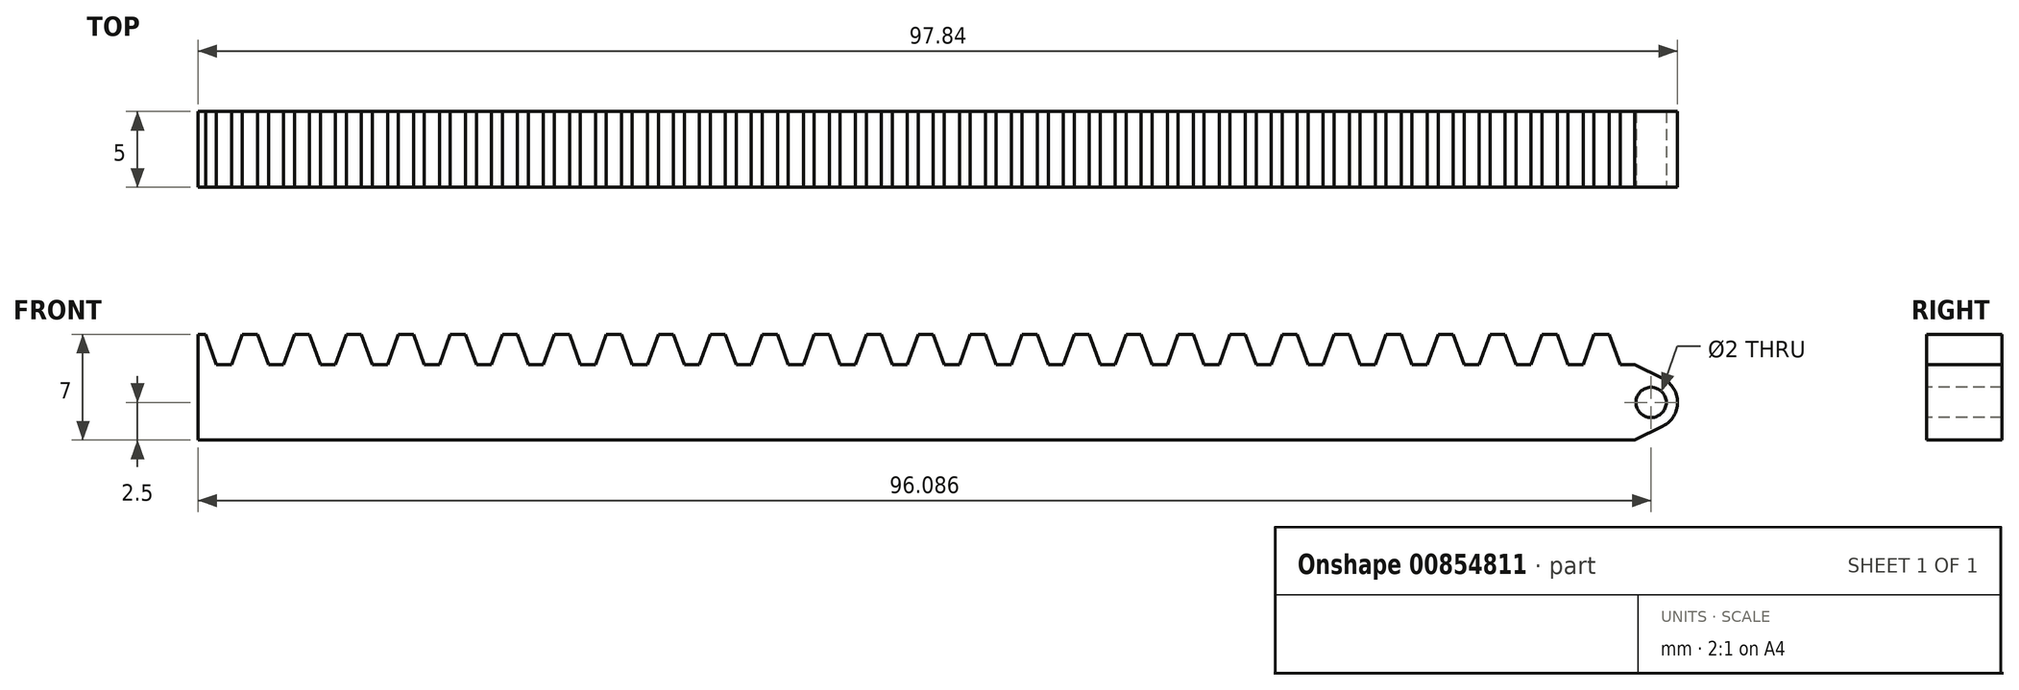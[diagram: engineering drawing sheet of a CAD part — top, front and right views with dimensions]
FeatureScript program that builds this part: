
annotation { "Feature Type Name" : "Feature", "Feature Type Description" : "" }
export const myFeature = defineFeature(function(context is Context, id is Id, definition is map)
    precondition{}
    {
        {
            var Q0;
            Q0=qCreatedBy(makeId("Front.planeOp"),FACE);
            var sketch = newSketch(context, id + "F0", { "sketchPlane" : qUnion([Q0])});
            skLineSegment(sketch, "E0", {"start": v(-54.36, 0) * mm, "end": v(55.64, 0) * mm});
            skLineSegment(sketch, "E1", {"start": v(-54.36, 0) * mm, "end": v(-54.36, 2) * mm});
            skLineSegment(sketch, "E2", {"start": v(-50.92, 4.03) * mm, "end": v(-50.92, 2) * mm, "construction": true});
            skLineSegment(sketch, "E3.MirrorCS", {"start": v(-47.49, 2) * mm, "end": v(-50.92, 2) * mm, "construction": true});
            skLineSegment(sketch, "E4", {"start": v(-54.36, 2) * mm, "end": v(-54.36, 3.15) * mm, "construction": true});
            skLineSegment(sketch, "E5", {"start": v(-54.36, 2) * mm, "end": v(-53.86, 2) * mm});
            skLineSegment(sketch, "E6", {"start": v(-52.64, 0) * mm, "end": v(-52.14, 0) * mm});
            skLineSegment(sketch, "E7", {"start": v(-52.64, 0) * mm, "end": v(-53.14, 0) * mm});
            skLineSegment(sketch, "E8", {"start": v(-50.92, 2) * mm, "end": v(-51.42, 2) * mm});
            skLineSegment(sketch, "E9", {"start": v(-54.36, 3.15) * mm, "end": v(-50.92, 3.15) * mm, "construction": true});
            skLineSegment(sketch, "E10", {"start": v(-52.64, 3.15) * mm, "end": v(-52.64, -0.78) * mm, "construction": true});
            skLineSegment(sketch, "E11", {"start": v(-53.86, 2) * mm, "end": v(-53.14, 0) * mm});
            skLineSegment(sketch, "E12", {"start": v(-52.14, 0) * mm, "end": v(-51.42, 2) * mm});
            skLineSegment(sketch, "E13.1.0.0", {"start": v(-48.7, 0) * mm, "end": v(-47.99, 2) * mm});
            skLineSegment(sketch, "E13.1.0.1", {"start": v(-50.92, 2) * mm, "end": v(-50.42, 2) * mm});
            skLineSegment(sketch, "E13.1.0.2", {"start": v(-50.42, 2) * mm, "end": v(-49.7, 0) * mm});
            skLineSegment(sketch, "E13.1.0.3", {"start": v(-49.2, 0) * mm, "end": v(-49.7, 0) * mm});
            skLineSegment(sketch, "E13.1.0.4", {"start": v(-49.2, 0) * mm, "end": v(-48.7, 0) * mm});
            skLineSegment(sketch, "E13.1.0.5", {"start": v(-47.49, 2) * mm, "end": v(-47.99, 2) * mm});
            skLineSegment(sketch, "E13.2.0.0", {"start": v(-45.27, 0) * mm, "end": v(-44.55, 2) * mm});
            skLineSegment(sketch, "E13.2.0.1", {"start": v(-47.49, 2) * mm, "end": v(-46.99, 2) * mm});
            skLineSegment(sketch, "E13.2.0.2", {"start": v(-46.99, 2) * mm, "end": v(-46.27, 0) * mm});
            skLineSegment(sketch, "E13.2.0.3", {"start": v(-45.77, 0) * mm, "end": v(-46.27, 0) * mm});
            skLineSegment(sketch, "E13.2.0.4", {"start": v(-45.77, 0) * mm, "end": v(-45.27, 0) * mm});
            skLineSegment(sketch, "E13.2.0.5", {"start": v(-44.05, 2) * mm, "end": v(-44.55, 2) * mm});
            skLineSegment(sketch, "E13.3.0.0", {"start": v(-41.83, 0) * mm, "end": v(-41.11, 2) * mm});
            skLineSegment(sketch, "E13.3.0.1", {"start": v(-44.05, 2) * mm, "end": v(-43.55, 2) * mm});
            skLineSegment(sketch, "E13.3.0.2", {"start": v(-43.55, 2) * mm, "end": v(-42.83, 0) * mm});
            skLineSegment(sketch, "E13.3.0.3", {"start": v(-42.33, 0) * mm, "end": v(-42.83, 0) * mm});
            skLineSegment(sketch, "E13.3.0.4", {"start": v(-42.33, 0) * mm, "end": v(-41.83, 0) * mm});
            skLineSegment(sketch, "E13.3.0.5", {"start": v(-40.61, 2) * mm, "end": v(-41.11, 2) * mm});
            skLineSegment(sketch, "E13.4.0.0", {"start": v(-38.4, 0) * mm, "end": v(-37.67, 2) * mm});
            skLineSegment(sketch, "E13.4.0.1", {"start": v(-40.61, 2) * mm, "end": v(-40.11, 2) * mm});
            skLineSegment(sketch, "E13.4.0.2", {"start": v(-40.11, 2) * mm, "end": v(-39.4, 0) * mm});
            skLineSegment(sketch, "E13.4.0.3", {"start": v(-38.9, 0) * mm, "end": v(-39.4, 0) * mm});
            skLineSegment(sketch, "E13.4.0.4", {"start": v(-38.9, 0) * mm, "end": v(-38.4, 0) * mm});
            skLineSegment(sketch, "E13.4.0.5", {"start": v(-37.17, 2) * mm, "end": v(-37.67, 2) * mm});
            skLineSegment(sketch, "E13.5.0.0", {"start": v(-34.95, 0) * mm, "end": v(-34.24, 2) * mm});
            skLineSegment(sketch, "E13.5.0.1", {"start": v(-37.17, 2) * mm, "end": v(-36.67, 2) * mm});
            skLineSegment(sketch, "E13.5.0.2", {"start": v(-36.67, 2) * mm, "end": v(-35.95, 0) * mm});
            skLineSegment(sketch, "E13.5.0.3", {"start": v(-35.45, 0) * mm, "end": v(-35.95, 0) * mm});
            skLineSegment(sketch, "E13.5.0.4", {"start": v(-35.45, 0) * mm, "end": v(-34.95, 0) * mm});
            skLineSegment(sketch, "E13.5.0.5", {"start": v(-33.74, 2) * mm, "end": v(-34.24, 2) * mm});
            skLineSegment(sketch, "E13.6.0.0", {"start": v(-31.52, 0) * mm, "end": v(-30.8, 2) * mm});
            skLineSegment(sketch, "E13.6.0.1", {"start": v(-33.74, 2) * mm, "end": v(-33.24, 2) * mm});
            skLineSegment(sketch, "E13.6.0.2", {"start": v(-33.24, 2) * mm, "end": v(-32.52, 0) * mm});
            skLineSegment(sketch, "E13.6.0.3", {"start": v(-32.02, 0) * mm, "end": v(-32.52, 0) * mm});
            skLineSegment(sketch, "E13.6.0.4", {"start": v(-32.02, 0) * mm, "end": v(-31.52, 0) * mm});
            skLineSegment(sketch, "E13.6.0.5", {"start": v(-30.3, 2) * mm, "end": v(-30.8, 2) * mm});
            skLineSegment(sketch, "E13.7.0.0", {"start": v(-28.08, 0) * mm, "end": v(-27.36, 2) * mm});
            skLineSegment(sketch, "E13.7.0.1", {"start": v(-30.3, 2) * mm, "end": v(-29.8, 2) * mm});
            skLineSegment(sketch, "E13.7.0.2", {"start": v(-29.8, 2) * mm, "end": v(-29.08, 0) * mm});
            skLineSegment(sketch, "E13.7.0.3", {"start": v(-28.58, 0) * mm, "end": v(-29.08, 0) * mm});
            skLineSegment(sketch, "E13.7.0.4", {"start": v(-28.58, 0) * mm, "end": v(-28.08, 0) * mm});
            skLineSegment(sketch, "E13.7.0.5", {"start": v(-26.86, 2) * mm, "end": v(-27.36, 2) * mm});
            skLineSegment(sketch, "E13.8.0.0", {"start": v(-24.64, 0) * mm, "end": v(-23.92, 2) * mm});
            skLineSegment(sketch, "E13.8.0.1", {"start": v(-26.86, 2) * mm, "end": v(-26.36, 2) * mm});
            skLineSegment(sketch, "E13.8.0.2", {"start": v(-26.36, 2) * mm, "end": v(-25.64, 0) * mm});
            skLineSegment(sketch, "E13.8.0.3", {"start": v(-25.14, 0) * mm, "end": v(-25.64, 0) * mm});
            skLineSegment(sketch, "E13.8.0.4", {"start": v(-25.14, 0) * mm, "end": v(-24.64, 0) * mm});
            skLineSegment(sketch, "E13.8.0.5", {"start": v(-23.42, 2) * mm, "end": v(-23.92, 2) * mm});
            skLineSegment(sketch, "E13.9.0.0", {"start": v(-21.2, 0) * mm, "end": v(-20.49, 2) * mm});
            skLineSegment(sketch, "E13.9.0.1", {"start": v(-23.42, 2) * mm, "end": v(-22.92, 2) * mm});
            skLineSegment(sketch, "E13.9.0.2", {"start": v(-22.92, 2) * mm, "end": v(-22.2, 0) * mm});
            skLineSegment(sketch, "E13.9.0.3", {"start": v(-21.7, 0) * mm, "end": v(-22.2, 0) * mm});
            skLineSegment(sketch, "E13.9.0.4", {"start": v(-21.7, 0) * mm, "end": v(-21.2, 0) * mm});
            skLineSegment(sketch, "E13.9.0.5", {"start": v(-19.99, 2) * mm, "end": v(-20.49, 2) * mm});
            skLineSegment(sketch, "E13.10.0.0", {"start": v(-17.77, 0) * mm, "end": v(-17.05, 2) * mm});
            skLineSegment(sketch, "E13.10.0.1", {"start": v(-19.99, 2) * mm, "end": v(-19.49, 2) * mm});
            skLineSegment(sketch, "E13.10.0.2", {"start": v(-19.49, 2) * mm, "end": v(-18.77, 0) * mm});
            skLineSegment(sketch, "E13.10.0.3", {"start": v(-18.27, 0) * mm, "end": v(-18.77, 0) * mm});
            skLineSegment(sketch, "E13.10.0.4", {"start": v(-18.27, 0) * mm, "end": v(-17.77, 0) * mm});
            skLineSegment(sketch, "E13.10.0.5", {"start": v(-16.55, 2) * mm, "end": v(-17.05, 2) * mm});
            skLineSegment(sketch, "E13.11.0.0", {"start": v(-14.33, 0) * mm, "end": v(-13.61, 2) * mm});
            skLineSegment(sketch, "E13.11.0.1", {"start": v(-16.55, 2) * mm, "end": v(-16.05, 2) * mm});
            skLineSegment(sketch, "E13.11.0.2", {"start": v(-16.05, 2) * mm, "end": v(-15.33, 0) * mm});
            skLineSegment(sketch, "E13.11.0.3", {"start": v(-14.83, 0) * mm, "end": v(-15.33, 0) * mm});
            skLineSegment(sketch, "E13.11.0.4", {"start": v(-14.83, 0) * mm, "end": v(-14.33, 0) * mm});
            skLineSegment(sketch, "E13.11.0.5", {"start": v(-13.11, 2) * mm, "end": v(-13.61, 2) * mm});
            skLineSegment(sketch, "E13.12.0.0", {"start": v(-10.9, 0) * mm, "end": v(-10.17, 2) * mm});
            skLineSegment(sketch, "E13.12.0.1", {"start": v(-13.11, 2) * mm, "end": v(-12.61, 2) * mm});
            skLineSegment(sketch, "E13.12.0.2", {"start": v(-12.61, 2) * mm, "end": v(-11.9, 0) * mm});
            skLineSegment(sketch, "E13.12.0.3", {"start": v(-11.4, 0) * mm, "end": v(-11.9, 0) * mm});
            skLineSegment(sketch, "E13.12.0.4", {"start": v(-11.4, 0) * mm, "end": v(-10.9, 0) * mm});
            skLineSegment(sketch, "E13.12.0.5", {"start": v(-9.67, 2) * mm, "end": v(-10.17, 2) * mm});
            skLineSegment(sketch, "E13.13.0.0", {"start": v(-7.45, 0) * mm, "end": v(-6.74, 2) * mm});
            skLineSegment(sketch, "E13.13.0.1", {"start": v(-9.67, 2) * mm, "end": v(-9.17, 2) * mm});
            skLineSegment(sketch, "E13.13.0.2", {"start": v(-9.17, 2) * mm, "end": v(-8.45, 0) * mm});
            skLineSegment(sketch, "E13.13.0.3", {"start": v(-7.95, 0) * mm, "end": v(-8.45, 0) * mm});
            skLineSegment(sketch, "E13.13.0.4", {"start": v(-7.95, 0) * mm, "end": v(-7.45, 0) * mm});
            skLineSegment(sketch, "E13.13.0.5", {"start": v(-6.24, 2) * mm, "end": v(-6.74, 2) * mm});
            skLineSegment(sketch, "E13.14.0.0", {"start": v(-4.02, 0) * mm, "end": v(-3.3, 2) * mm});
            skLineSegment(sketch, "E13.14.0.1", {"start": v(-6.24, 2) * mm, "end": v(-5.74, 2) * mm});
            skLineSegment(sketch, "E13.14.0.2", {"start": v(-5.74, 2) * mm, "end": v(-5.02, 0) * mm});
            skLineSegment(sketch, "E13.14.0.3", {"start": v(-4.52, 0) * mm, "end": v(-5.02, 0) * mm});
            skLineSegment(sketch, "E13.14.0.4", {"start": v(-4.52, 0) * mm, "end": v(-4.02, 0) * mm});
            skLineSegment(sketch, "E13.14.0.5", {"start": v(-2.8, 2) * mm, "end": v(-3.3, 2) * mm});
            skLineSegment(sketch, "E13.15.0.0", {"start": v(-0.58, 0) * mm, "end": v(0.14, 2) * mm});
            skLineSegment(sketch, "E13.15.0.1", {"start": v(-2.8, 2) * mm, "end": v(-2.3, 2) * mm});
            skLineSegment(sketch, "E13.15.0.2", {"start": v(-2.3, 2) * mm, "end": v(-1.58, 0) * mm});
            skLineSegment(sketch, "E13.15.0.3", {"start": v(-1.08, 0) * mm, "end": v(-1.58, 0) * mm});
            skLineSegment(sketch, "E13.15.0.4", {"start": v(-1.08, 0) * mm, "end": v(-0.58, 0) * mm});
            skLineSegment(sketch, "E13.15.0.5", {"start": v(0.64, 2) * mm, "end": v(0.14, 2) * mm});
            skLineSegment(sketch, "E13.16.0.0", {"start": v(2.86, 0) * mm, "end": v(3.58, 2) * mm});
            skLineSegment(sketch, "E13.16.0.1", {"start": v(0.64, 2) * mm, "end": v(1.14, 2) * mm});
            skLineSegment(sketch, "E13.16.0.2", {"start": v(1.14, 2) * mm, "end": v(1.86, 0) * mm});
            skLineSegment(sketch, "E13.16.0.3", {"start": v(2.36, 0) * mm, "end": v(1.86, 0) * mm});
            skLineSegment(sketch, "E13.16.0.4", {"start": v(2.36, 0) * mm, "end": v(2.86, 0) * mm});
            skLineSegment(sketch, "E13.16.0.5", {"start": v(4.08, 2) * mm, "end": v(3.58, 2) * mm});
            skLineSegment(sketch, "E13.17.0.0", {"start": v(6.3, 0) * mm, "end": v(7.01, 2) * mm});
            skLineSegment(sketch, "E13.17.0.1", {"start": v(4.08, 2) * mm, "end": v(4.58, 2) * mm});
            skLineSegment(sketch, "E13.17.0.2", {"start": v(4.58, 2) * mm, "end": v(5.3, 0) * mm});
            skLineSegment(sketch, "E13.17.0.3", {"start": v(5.8, 0) * mm, "end": v(5.3, 0) * mm});
            skLineSegment(sketch, "E13.17.0.4", {"start": v(5.8, 0) * mm, "end": v(6.3, 0) * mm});
            skLineSegment(sketch, "E13.17.0.5", {"start": v(7.51, 2) * mm, "end": v(7.01, 2) * mm});
            skLineSegment(sketch, "E13.18.0.0", {"start": v(9.73, 0) * mm, "end": v(10.45, 2) * mm});
            skLineSegment(sketch, "E13.18.0.1", {"start": v(7.51, 2) * mm, "end": v(8.01, 2) * mm});
            skLineSegment(sketch, "E13.18.0.2", {"start": v(8.01, 2) * mm, "end": v(8.73, 0) * mm});
            skLineSegment(sketch, "E13.18.0.3", {"start": v(9.23, 0) * mm, "end": v(8.73, 0) * mm});
            skLineSegment(sketch, "E13.18.0.4", {"start": v(9.23, 0) * mm, "end": v(9.73, 0) * mm});
            skLineSegment(sketch, "E13.18.0.5", {"start": v(10.95, 2) * mm, "end": v(10.45, 2) * mm});
            skLineSegment(sketch, "E13.19.0.0", {"start": v(13.17, 0) * mm, "end": v(13.89, 2) * mm});
            skLineSegment(sketch, "E13.19.0.1", {"start": v(10.95, 2) * mm, "end": v(11.45, 2) * mm});
            skLineSegment(sketch, "E13.19.0.2", {"start": v(11.45, 2) * mm, "end": v(12.17, 0) * mm});
            skLineSegment(sketch, "E13.19.0.3", {"start": v(12.67, 0) * mm, "end": v(12.17, 0) * mm});
            skLineSegment(sketch, "E13.19.0.4", {"start": v(12.67, 0) * mm, "end": v(13.17, 0) * mm});
            skLineSegment(sketch, "E13.19.0.5", {"start": v(14.39, 2) * mm, "end": v(13.89, 2) * mm});
            skLineSegment(sketch, "E13.20.0.0", {"start": v(16.6, 0) * mm, "end": v(17.33, 2) * mm});
            skLineSegment(sketch, "E13.20.0.1", {"start": v(14.39, 2) * mm, "end": v(14.89, 2) * mm});
            skLineSegment(sketch, "E13.20.0.2", {"start": v(14.89, 2) * mm, "end": v(15.6, 0) * mm});
            skLineSegment(sketch, "E13.20.0.3", {"start": v(16.1, 0) * mm, "end": v(15.6, 0) * mm});
            skLineSegment(sketch, "E13.20.0.4", {"start": v(16.1, 0) * mm, "end": v(16.6, 0) * mm});
            skLineSegment(sketch, "E13.20.0.5", {"start": v(17.83, 2) * mm, "end": v(17.33, 2) * mm});
            skLineSegment(sketch, "E13.21.0.0", {"start": v(20.05, 0) * mm, "end": v(20.76, 2) * mm});
            skLineSegment(sketch, "E13.21.0.1", {"start": v(17.83, 2) * mm, "end": v(18.33, 2) * mm});
            skLineSegment(sketch, "E13.21.0.2", {"start": v(18.33, 2) * mm, "end": v(19.05, 0) * mm});
            skLineSegment(sketch, "E13.21.0.3", {"start": v(19.55, 0) * mm, "end": v(19.05, 0) * mm});
            skLineSegment(sketch, "E13.21.0.4", {"start": v(19.55, 0) * mm, "end": v(20.05, 0) * mm});
            skLineSegment(sketch, "E13.21.0.5", {"start": v(21.26, 2) * mm, "end": v(20.76, 2) * mm});
            skLineSegment(sketch, "E13.22.0.0", {"start": v(23.48, 0) * mm, "end": v(24.2, 2) * mm});
            skLineSegment(sketch, "E13.22.0.1", {"start": v(21.26, 2) * mm, "end": v(21.76, 2) * mm});
            skLineSegment(sketch, "E13.22.0.2", {"start": v(21.76, 2) * mm, "end": v(22.48, 0) * mm});
            skLineSegment(sketch, "E13.22.0.3", {"start": v(22.98, 0) * mm, "end": v(22.48, 0) * mm});
            skLineSegment(sketch, "E13.22.0.4", {"start": v(22.98, 0) * mm, "end": v(23.48, 0) * mm});
            skLineSegment(sketch, "E13.22.0.5", {"start": v(24.7, 2) * mm, "end": v(24.2, 2) * mm});
            skLineSegment(sketch, "E13.23.0.0", {"start": v(26.92, 0) * mm, "end": v(27.64, 2) * mm});
            skLineSegment(sketch, "E13.23.0.1", {"start": v(24.7, 2) * mm, "end": v(25.2, 2) * mm});
            skLineSegment(sketch, "E13.23.0.2", {"start": v(25.2, 2) * mm, "end": v(25.92, 0) * mm});
            skLineSegment(sketch, "E13.23.0.3", {"start": v(26.42, 0) * mm, "end": v(25.92, 0) * mm});
            skLineSegment(sketch, "E13.23.0.4", {"start": v(26.42, 0) * mm, "end": v(26.92, 0) * mm});
            skLineSegment(sketch, "E13.23.0.5", {"start": v(28.14, 2) * mm, "end": v(27.64, 2) * mm});
            skLineSegment(sketch, "E13.24.0.0", {"start": v(30.36, 0) * mm, "end": v(31.08, 2) * mm});
            skLineSegment(sketch, "E13.24.0.1", {"start": v(28.14, 2) * mm, "end": v(28.64, 2) * mm});
            skLineSegment(sketch, "E13.24.0.2", {"start": v(28.64, 2) * mm, "end": v(29.36, 0) * mm});
            skLineSegment(sketch, "E13.24.0.3", {"start": v(29.86, 0) * mm, "end": v(29.36, 0) * mm});
            skLineSegment(sketch, "E13.24.0.4", {"start": v(29.86, 0) * mm, "end": v(30.36, 0) * mm});
            skLineSegment(sketch, "E13.24.0.5", {"start": v(31.58, 2) * mm, "end": v(31.08, 2) * mm});
            skLineSegment(sketch, "E13.25.0.0", {"start": v(33.8, 0) * mm, "end": v(34.51, 2) * mm});
            skLineSegment(sketch, "E13.25.0.1", {"start": v(31.58, 2) * mm, "end": v(32.08, 2) * mm});
            skLineSegment(sketch, "E13.25.0.2", {"start": v(32.08, 2) * mm, "end": v(32.8, 0) * mm});
            skLineSegment(sketch, "E13.25.0.3", {"start": v(33.3, 0) * mm, "end": v(32.8, 0) * mm});
            skLineSegment(sketch, "E13.25.0.4", {"start": v(33.3, 0) * mm, "end": v(33.8, 0) * mm});
            skLineSegment(sketch, "E13.25.0.5", {"start": v(35.01, 2) * mm, "end": v(34.51, 2) * mm});
            skLineSegment(sketch, "E13.26.0.0", {"start": v(37.23, 0) * mm, "end": v(37.95, 2) * mm});
            skLineSegment(sketch, "E13.26.0.1", {"start": v(35.01, 2) * mm, "end": v(35.51, 2) * mm});
            skLineSegment(sketch, "E13.26.0.2", {"start": v(35.51, 2) * mm, "end": v(36.23, 0) * mm});
            skLineSegment(sketch, "E13.26.0.3", {"start": v(36.73, 0) * mm, "end": v(36.23, 0) * mm});
            skLineSegment(sketch, "E13.26.0.4", {"start": v(36.73, 0) * mm, "end": v(37.23, 0) * mm});
            skLineSegment(sketch, "E13.26.0.5", {"start": v(38.45, 2) * mm, "end": v(37.95, 2) * mm});
            skLineSegment(sketch, "E13.27.0.0", {"start": v(40.67, 0) * mm, "end": v(41.39, 2) * mm});
            skLineSegment(sketch, "E13.27.0.1", {"start": v(38.45, 2) * mm, "end": v(38.95, 2) * mm});
            skLineSegment(sketch, "E13.27.0.2", {"start": v(38.95, 2) * mm, "end": v(39.67, 0) * mm});
            skLineSegment(sketch, "E13.27.0.3", {"start": v(40.17, 0) * mm, "end": v(39.67, 0) * mm});
            skLineSegment(sketch, "E13.27.0.4", {"start": v(40.17, 0) * mm, "end": v(40.67, 0) * mm});
            skLineSegment(sketch, "E13.27.0.5", {"start": v(41.89, 2) * mm, "end": v(41.39, 2) * mm});
            skLineSegment(sketch, "E13.28.0.0", {"start": v(44.1, 0) * mm, "end": v(44.83, 2) * mm});
            skLineSegment(sketch, "E13.28.0.1", {"start": v(41.89, 2) * mm, "end": v(42.39, 2) * mm});
            skLineSegment(sketch, "E13.28.0.2", {"start": v(42.39, 2) * mm, "end": v(43.1, 0) * mm});
            skLineSegment(sketch, "E13.28.0.3", {"start": v(43.6, 0) * mm, "end": v(43.1, 0) * mm});
            skLineSegment(sketch, "E13.28.0.4", {"start": v(43.6, 0) * mm, "end": v(44.1, 0) * mm});
            skLineSegment(sketch, "E13.28.0.5", {"start": v(45.33, 2) * mm, "end": v(44.83, 2) * mm});
            skLineSegment(sketch, "E13.29.0.0", {"start": v(47.55, 0) * mm, "end": v(48.26, 2) * mm});
            skLineSegment(sketch, "E13.29.0.1", {"start": v(45.33, 2) * mm, "end": v(45.83, 2) * mm});
            skLineSegment(sketch, "E13.29.0.2", {"start": v(45.83, 2) * mm, "end": v(46.55, 0) * mm});
            skLineSegment(sketch, "E13.29.0.3", {"start": v(47.05, 0) * mm, "end": v(46.55, 0) * mm});
            skLineSegment(sketch, "E13.29.0.4", {"start": v(47.05, 0) * mm, "end": v(47.55, 0) * mm});
            skLineSegment(sketch, "E13.29.0.5", {"start": v(48.76, 2) * mm, "end": v(48.26, 2) * mm});
            skLineSegment(sketch, "E13.30.0.0", {"start": v(50.98, 0) * mm, "end": v(51.7, 2) * mm});
            skLineSegment(sketch, "E13.30.0.1", {"start": v(48.76, 2) * mm, "end": v(49.26, 2) * mm});
            skLineSegment(sketch, "E13.30.0.2", {"start": v(49.26, 2) * mm, "end": v(49.98, 0) * mm});
            skLineSegment(sketch, "E13.30.0.3", {"start": v(50.48, 0) * mm, "end": v(49.98, 0) * mm});
            skLineSegment(sketch, "E13.30.0.4", {"start": v(50.48, 0) * mm, "end": v(50.98, 0) * mm});
            skLineSegment(sketch, "E13.30.0.5", {"start": v(52.2, 2) * mm, "end": v(51.7, 2) * mm});
            skLineSegment(sketch, "E13.31.0.0", {"start": v(54.42, 0) * mm, "end": v(55.14, 2) * mm});
            skLineSegment(sketch, "E13.31.0.1", {"start": v(52.2, 2) * mm, "end": v(52.7, 2) * mm});
            skLineSegment(sketch, "E13.31.0.2", {"start": v(52.7, 2) * mm, "end": v(53.42, 0) * mm});
            skLineSegment(sketch, "E13.31.0.3", {"start": v(53.92, 0) * mm, "end": v(53.42, 0) * mm});
            skLineSegment(sketch, "E13.31.0.4", {"start": v(53.92, 0) * mm, "end": v(54.42, 0) * mm});
            skLineSegment(sketch, "E13.31.0.5", {"start": v(55.64, 2) * mm, "end": v(55.14, 2) * mm});
            skLineSegment(sketch, "E13.direction1", {"start": v(-53.14, 0) * mm, "end": v(-49.7, 0) * mm, "construction": true});
            skLineSegment(sketch, "E14", {"start": v(-54.36, 0) * mm, "end": v(-54.36, -5) * mm});
            skLineSegment(sketch, "E15", {"start": v(-54.36, -5) * mm, "end": v(55.64, -5) * mm});
            skLineSegment(sketch, "E16", {"start": v(55.64, -5) * mm, "end": v(55.64, 2) * mm});
            skSolve(sketch);
        }
        {
            var Q0;
            Q0 = qSketchRegion(id + "F0", true);
            extrude(context, id + "F1", {"entities" : qUnion([Q0]), "depth" : 5 * mm, "offsetDistance" : 25 * mm});
        }
        {
            var Q0;
            Q0=makeQuery(id+"F1.opExtrude","CAP_FACE",FACE,{"disambiguationData":[OSD([sQuery(id+"F0.wireOp",EDGE,"E1"),sQuery(id+"F0.wireOp",EDGE,"E5"),sQuery(id+"F0.wireOp",EDGE,"E6"),sQuery(id+"F0.wireOp",EDGE,"E7"),sQuery(id+"F0.wireOp",EDGE,"E8"),sQuery(id+"F0.wireOp",EDGE,"E11"),sQuery(id+"F0.wireOp",EDGE,"E12"),sQuery(id+"F0.wireOp",EDGE,"E13.1.0.0"),sQuery(id+"F0.wireOp",EDGE,"E13.1.0.1"),sQuery(id+"F0.wireOp",EDGE,"E13.1.0.2"),sQuery(id+"F0.wireOp",EDGE,"E13.1.0.3"),sQuery(id+"F0.wireOp",EDGE,"E13.1.0.4"),sQuery(id+"F0.wireOp",EDGE,"E13.1.0.5"),sQuery(id+"F0.wireOp",EDGE,"E13.2.0.0"),sQuery(id+"F0.wireOp",EDGE,"E13.2.0.1"),sQuery(id+"F0.wireOp",EDGE,"E13.2.0.2"),sQuery(id+"F0.wireOp",EDGE,"E13.2.0.3"),sQuery(id+"F0.wireOp",EDGE,"E13.2.0.4"),sQuery(id+"F0.wireOp",EDGE,"E13.2.0.5"),sQuery(id+"F0.wireOp",EDGE,"E13.3.0.0"),sQuery(id+"F0.wireOp",EDGE,"E13.3.0.1"),sQuery(id+"F0.wireOp",EDGE,"E13.3.0.2"),sQuery(id+"F0.wireOp",EDGE,"E13.3.0.3"),sQuery(id+"F0.wireOp",EDGE,"E13.3.0.4"),sQuery(id+"F0.wireOp",EDGE,"E13.3.0.5"),sQuery(id+"F0.wireOp",EDGE,"E13.4.0.0"),sQuery(id+"F0.wireOp",EDGE,"E13.4.0.1"),sQuery(id+"F0.wireOp",EDGE,"E13.4.0.2"),sQuery(id+"F0.wireOp",EDGE,"E13.4.0.3"),sQuery(id+"F0.wireOp",EDGE,"E13.4.0.4"),sQuery(id+"F0.wireOp",EDGE,"E13.4.0.5"),sQuery(id+"F0.wireOp",EDGE,"E13.5.0.0"),sQuery(id+"F0.wireOp",EDGE,"E13.5.0.1"),sQuery(id+"F0.wireOp",EDGE,"E13.5.0.2"),sQuery(id+"F0.wireOp",EDGE,"E13.5.0.3"),sQuery(id+"F0.wireOp",EDGE,"E13.5.0.4"),sQuery(id+"F0.wireOp",EDGE,"E13.5.0.5"),sQuery(id+"F0.wireOp",EDGE,"E13.6.0.0"),sQuery(id+"F0.wireOp",EDGE,"E13.6.0.1"),sQuery(id+"F0.wireOp",EDGE,"E13.6.0.2"),sQuery(id+"F0.wireOp",EDGE,"E13.6.0.3"),sQuery(id+"F0.wireOp",EDGE,"E13.6.0.4"),sQuery(id+"F0.wireOp",EDGE,"E13.6.0.5"),sQuery(id+"F0.wireOp",EDGE,"E13.7.0.0"),sQuery(id+"F0.wireOp",EDGE,"E13.7.0.1"),sQuery(id+"F0.wireOp",EDGE,"E13.7.0.2"),sQuery(id+"F0.wireOp",EDGE,"E13.7.0.3"),sQuery(id+"F0.wireOp",EDGE,"E13.7.0.4"),sQuery(id+"F0.wireOp",EDGE,"E13.7.0.5"),sQuery(id+"F0.wireOp",EDGE,"E13.8.0.0"),sQuery(id+"F0.wireOp",EDGE,"E13.8.0.1"),sQuery(id+"F0.wireOp",EDGE,"E13.8.0.2"),sQuery(id+"F0.wireOp",EDGE,"E13.8.0.3"),sQuery(id+"F0.wireOp",EDGE,"E13.8.0.4"),sQuery(id+"F0.wireOp",EDGE,"E13.8.0.5"),sQuery(id+"F0.wireOp",EDGE,"E13.9.0.0"),sQuery(id+"F0.wireOp",EDGE,"E13.9.0.1"),sQuery(id+"F0.wireOp",EDGE,"E13.9.0.2"),sQuery(id+"F0.wireOp",EDGE,"E13.9.0.3"),sQuery(id+"F0.wireOp",EDGE,"E13.9.0.4"),sQuery(id+"F0.wireOp",EDGE,"E13.9.0.5"),sQuery(id+"F0.wireOp",EDGE,"E13.10.0.0"),sQuery(id+"F0.wireOp",EDGE,"E13.10.0.1"),sQuery(id+"F0.wireOp",EDGE,"E13.10.0.2"),sQuery(id+"F0.wireOp",EDGE,"E13.10.0.3"),sQuery(id+"F0.wireOp",EDGE,"E13.10.0.4"),sQuery(id+"F0.wireOp",EDGE,"E13.10.0.5"),sQuery(id+"F0.wireOp",EDGE,"E13.11.0.0"),sQuery(id+"F0.wireOp",EDGE,"E13.11.0.1"),sQuery(id+"F0.wireOp",EDGE,"E13.11.0.2"),sQuery(id+"F0.wireOp",EDGE,"E13.11.0.3"),sQuery(id+"F0.wireOp",EDGE,"E13.11.0.4"),sQuery(id+"F0.wireOp",EDGE,"E13.11.0.5"),sQuery(id+"F0.wireOp",EDGE,"E13.12.0.0"),sQuery(id+"F0.wireOp",EDGE,"E13.12.0.1"),sQuery(id+"F0.wireOp",EDGE,"E13.12.0.2"),sQuery(id+"F0.wireOp",EDGE,"E13.12.0.3"),sQuery(id+"F0.wireOp",EDGE,"E13.12.0.4"),sQuery(id+"F0.wireOp",EDGE,"E13.12.0.5"),sQuery(id+"F0.wireOp",EDGE,"E13.13.0.0"),sQuery(id+"F0.wireOp",EDGE,"E13.13.0.1"),sQuery(id+"F0.wireOp",EDGE,"E13.13.0.2"),sQuery(id+"F0.wireOp",EDGE,"E13.13.0.3"),sQuery(id+"F0.wireOp",EDGE,"E13.13.0.4"),sQuery(id+"F0.wireOp",EDGE,"E13.13.0.5"),sQuery(id+"F0.wireOp",EDGE,"E13.14.0.0"),sQuery(id+"F0.wireOp",EDGE,"E13.14.0.1"),sQuery(id+"F0.wireOp",EDGE,"E13.14.0.2"),sQuery(id+"F0.wireOp",EDGE,"E13.14.0.3"),sQuery(id+"F0.wireOp",EDGE,"E13.14.0.4"),sQuery(id+"F0.wireOp",EDGE,"E13.14.0.5"),sQuery(id+"F0.wireOp",EDGE,"E13.15.0.0"),sQuery(id+"F0.wireOp",EDGE,"E13.15.0.1"),sQuery(id+"F0.wireOp",EDGE,"E13.15.0.2"),sQuery(id+"F0.wireOp",EDGE,"E13.15.0.3"),sQuery(id+"F0.wireOp",EDGE,"E13.15.0.4"),sQuery(id+"F0.wireOp",EDGE,"E13.15.0.5"),sQuery(id+"F0.wireOp",EDGE,"E13.16.0.0"),sQuery(id+"F0.wireOp",EDGE,"E13.16.0.1"),sQuery(id+"F0.wireOp",EDGE,"E13.16.0.2"),sQuery(id+"F0.wireOp",EDGE,"E13.16.0.3"),sQuery(id+"F0.wireOp",EDGE,"E13.16.0.4"),sQuery(id+"F0.wireOp",EDGE,"E13.16.0.5"),sQuery(id+"F0.wireOp",EDGE,"E13.17.0.0"),sQuery(id+"F0.wireOp",EDGE,"E13.17.0.1"),sQuery(id+"F0.wireOp",EDGE,"E13.17.0.2"),sQuery(id+"F0.wireOp",EDGE,"E13.17.0.3"),sQuery(id+"F0.wireOp",EDGE,"E13.17.0.4"),sQuery(id+"F0.wireOp",EDGE,"E13.17.0.5"),sQuery(id+"F0.wireOp",EDGE,"E13.18.0.0"),sQuery(id+"F0.wireOp",EDGE,"E13.18.0.1"),sQuery(id+"F0.wireOp",EDGE,"E13.18.0.2"),sQuery(id+"F0.wireOp",EDGE,"E13.18.0.3"),sQuery(id+"F0.wireOp",EDGE,"E13.18.0.4"),sQuery(id+"F0.wireOp",EDGE,"E13.18.0.5"),sQuery(id+"F0.wireOp",EDGE,"E13.19.0.0"),sQuery(id+"F0.wireOp",EDGE,"E13.19.0.1"),sQuery(id+"F0.wireOp",EDGE,"E13.19.0.2"),sQuery(id+"F0.wireOp",EDGE,"E13.19.0.3"),sQuery(id+"F0.wireOp",EDGE,"E13.19.0.4"),sQuery(id+"F0.wireOp",EDGE,"E13.19.0.5"),sQuery(id+"F0.wireOp",EDGE,"E13.20.0.0"),sQuery(id+"F0.wireOp",EDGE,"E13.20.0.1"),sQuery(id+"F0.wireOp",EDGE,"E13.20.0.2"),sQuery(id+"F0.wireOp",EDGE,"E13.20.0.3"),sQuery(id+"F0.wireOp",EDGE,"E13.20.0.4"),sQuery(id+"F0.wireOp",EDGE,"E13.20.0.5"),sQuery(id+"F0.wireOp",EDGE,"E13.21.0.0"),sQuery(id+"F0.wireOp",EDGE,"E13.21.0.1"),sQuery(id+"F0.wireOp",EDGE,"E13.21.0.2"),sQuery(id+"F0.wireOp",EDGE,"E13.21.0.3"),sQuery(id+"F0.wireOp",EDGE,"E13.21.0.4"),sQuery(id+"F0.wireOp",EDGE,"E13.21.0.5"),sQuery(id+"F0.wireOp",EDGE,"E13.22.0.0"),sQuery(id+"F0.wireOp",EDGE,"E13.22.0.1"),sQuery(id+"F0.wireOp",EDGE,"E13.22.0.2"),sQuery(id+"F0.wireOp",EDGE,"E13.22.0.3"),sQuery(id+"F0.wireOp",EDGE,"E13.22.0.4"),sQuery(id+"F0.wireOp",EDGE,"E13.22.0.5"),sQuery(id+"F0.wireOp",EDGE,"E13.23.0.0"),sQuery(id+"F0.wireOp",EDGE,"E13.23.0.1"),sQuery(id+"F0.wireOp",EDGE,"E13.23.0.2"),sQuery(id+"F0.wireOp",EDGE,"E13.23.0.3"),sQuery(id+"F0.wireOp",EDGE,"E13.23.0.4"),sQuery(id+"F0.wireOp",EDGE,"E13.23.0.5"),sQuery(id+"F0.wireOp",EDGE,"E13.24.0.0"),sQuery(id+"F0.wireOp",EDGE,"E13.24.0.1"),sQuery(id+"F0.wireOp",EDGE,"E13.24.0.2"),sQuery(id+"F0.wireOp",EDGE,"E13.24.0.3"),sQuery(id+"F0.wireOp",EDGE,"E13.24.0.4"),sQuery(id+"F0.wireOp",EDGE,"E13.24.0.5"),sQuery(id+"F0.wireOp",EDGE,"E13.25.0.0"),sQuery(id+"F0.wireOp",EDGE,"E13.25.0.1"),sQuery(id+"F0.wireOp",EDGE,"E13.25.0.2"),sQuery(id+"F0.wireOp",EDGE,"E13.25.0.3"),sQuery(id+"F0.wireOp",EDGE,"E13.25.0.4"),sQuery(id+"F0.wireOp",EDGE,"E13.25.0.5"),sQuery(id+"F0.wireOp",EDGE,"E13.26.0.0"),sQuery(id+"F0.wireOp",EDGE,"E13.26.0.1"),sQuery(id+"F0.wireOp",EDGE,"E13.26.0.2"),sQuery(id+"F0.wireOp",EDGE,"E13.26.0.3"),sQuery(id+"F0.wireOp",EDGE,"E13.26.0.4"),sQuery(id+"F0.wireOp",EDGE,"E13.26.0.5"),sQuery(id+"F0.wireOp",EDGE,"E13.27.0.0"),sQuery(id+"F0.wireOp",EDGE,"E13.27.0.1"),sQuery(id+"F0.wireOp",EDGE,"E13.27.0.2"),sQuery(id+"F0.wireOp",EDGE,"E13.27.0.3"),sQuery(id+"F0.wireOp",EDGE,"E13.27.0.4"),sQuery(id+"F0.wireOp",EDGE,"E13.27.0.5"),sQuery(id+"F0.wireOp",EDGE,"E13.28.0.0"),sQuery(id+"F0.wireOp",EDGE,"E13.28.0.1"),sQuery(id+"F0.wireOp",EDGE,"E13.28.0.2"),sQuery(id+"F0.wireOp",EDGE,"E13.28.0.3"),sQuery(id+"F0.wireOp",EDGE,"E13.28.0.4"),sQuery(id+"F0.wireOp",EDGE,"E13.28.0.5"),sQuery(id+"F0.wireOp",EDGE,"E13.29.0.0"),sQuery(id+"F0.wireOp",EDGE,"E13.29.0.1"),sQuery(id+"F0.wireOp",EDGE,"E13.29.0.2"),sQuery(id+"F0.wireOp",EDGE,"E13.29.0.3"),sQuery(id+"F0.wireOp",EDGE,"E13.29.0.4"),sQuery(id+"F0.wireOp",EDGE,"E13.29.0.5"),sQuery(id+"F0.wireOp",EDGE,"E13.30.0.0"),sQuery(id+"F0.wireOp",EDGE,"E13.30.0.1"),sQuery(id+"F0.wireOp",EDGE,"E13.30.0.2"),sQuery(id+"F0.wireOp",EDGE,"E13.30.0.3"),sQuery(id+"F0.wireOp",EDGE,"E13.30.0.4"),sQuery(id+"F0.wireOp",EDGE,"E13.30.0.5"),sQuery(id+"F0.wireOp",EDGE,"E13.31.0.0"),sQuery(id+"F0.wireOp",EDGE,"E13.31.0.1"),sQuery(id+"F0.wireOp",EDGE,"E13.31.0.2"),sQuery(id+"F0.wireOp",EDGE,"E13.31.0.3"),sQuery(id+"F0.wireOp",EDGE,"E13.31.0.4"),sQuery(id+"F0.wireOp",EDGE,"E13.31.0.5"),sQuery(id+"F0.wireOp",EDGE,"E14"),sQuery(id+"F0.wireOp",EDGE,"E15"),sQuery(id+"F0.wireOp",EDGE,"E16")])],"isStart":false});
            var sketch = newSketch(context, id + "F2", { "sketchPlane" : qUnion([Q0])});
            skLineSegment(sketch, "E17", {"start": v(-54.36, -5) * mm, "end": v(40.64, -5) * mm});
            skLineSegment(sketch, "E18", {"start": v(40.64, -5) * mm, "end": v(40.64, 9.7) * mm});
            skLineSegment(sketch, "E19", {"start": v(40.64, 9.7) * mm, "end": v(59.68, 9.7) * mm});
            skLineSegment(sketch, "E20", {"start": v(59.68, 9.7) * mm, "end": v(59.68, -8.51) * mm});
            skLineSegment(sketch, "E21", {"start": v(59.68, -8.51) * mm, "end": v(40.64, -8.51) * mm});
            skLineSegment(sketch, "E22", {"start": v(40.64, -8.51) * mm, "end": v(40.64, -5) * mm});
            skSolve(sketch);
        }
        {
            var Q0;
            Q0 = qSketchRegion(id + "F2", true);
            extrude(context, id + "F3", {"entities" : qUnion([Q0]), "operationType" : NewBodyOperationType.REMOVE, "oppositeDirection" : true, "depth" : 25 * mm, "offsetDistance" : 25 * mm});
        }
        {
            var Q0;
            Q0=makeQuery(id+"F1.opExtrude","CAP_FACE",FACE,{"disambiguationData":[OSD([sQuery(id+"F0.wireOp",EDGE,"E1"),sQuery(id+"F0.wireOp",EDGE,"E5"),sQuery(id+"F0.wireOp",EDGE,"E6"),sQuery(id+"F0.wireOp",EDGE,"E7"),sQuery(id+"F0.wireOp",EDGE,"E8"),sQuery(id+"F0.wireOp",EDGE,"E11"),sQuery(id+"F0.wireOp",EDGE,"E12"),sQuery(id+"F0.wireOp",EDGE,"E13.1.0.0"),sQuery(id+"F0.wireOp",EDGE,"E13.1.0.1"),sQuery(id+"F0.wireOp",EDGE,"E13.1.0.2"),sQuery(id+"F0.wireOp",EDGE,"E13.1.0.3"),sQuery(id+"F0.wireOp",EDGE,"E13.1.0.4"),sQuery(id+"F0.wireOp",EDGE,"E13.1.0.5"),sQuery(id+"F0.wireOp",EDGE,"E13.2.0.0"),sQuery(id+"F0.wireOp",EDGE,"E13.2.0.1"),sQuery(id+"F0.wireOp",EDGE,"E13.2.0.2"),sQuery(id+"F0.wireOp",EDGE,"E13.2.0.3"),sQuery(id+"F0.wireOp",EDGE,"E13.2.0.4"),sQuery(id+"F0.wireOp",EDGE,"E13.2.0.5"),sQuery(id+"F0.wireOp",EDGE,"E13.3.0.0"),sQuery(id+"F0.wireOp",EDGE,"E13.3.0.1"),sQuery(id+"F0.wireOp",EDGE,"E13.3.0.2"),sQuery(id+"F0.wireOp",EDGE,"E13.3.0.3"),sQuery(id+"F0.wireOp",EDGE,"E13.3.0.4"),sQuery(id+"F0.wireOp",EDGE,"E13.3.0.5"),sQuery(id+"F0.wireOp",EDGE,"E13.4.0.0"),sQuery(id+"F0.wireOp",EDGE,"E13.4.0.1"),sQuery(id+"F0.wireOp",EDGE,"E13.4.0.2"),sQuery(id+"F0.wireOp",EDGE,"E13.4.0.3"),sQuery(id+"F0.wireOp",EDGE,"E13.4.0.4"),sQuery(id+"F0.wireOp",EDGE,"E13.4.0.5"),sQuery(id+"F0.wireOp",EDGE,"E13.5.0.0"),sQuery(id+"F0.wireOp",EDGE,"E13.5.0.1"),sQuery(id+"F0.wireOp",EDGE,"E13.5.0.2"),sQuery(id+"F0.wireOp",EDGE,"E13.5.0.3"),sQuery(id+"F0.wireOp",EDGE,"E13.5.0.4"),sQuery(id+"F0.wireOp",EDGE,"E13.5.0.5"),sQuery(id+"F0.wireOp",EDGE,"E13.6.0.0"),sQuery(id+"F0.wireOp",EDGE,"E13.6.0.1"),sQuery(id+"F0.wireOp",EDGE,"E13.6.0.2"),sQuery(id+"F0.wireOp",EDGE,"E13.6.0.3"),sQuery(id+"F0.wireOp",EDGE,"E13.6.0.4"),sQuery(id+"F0.wireOp",EDGE,"E13.6.0.5"),sQuery(id+"F0.wireOp",EDGE,"E13.7.0.0"),sQuery(id+"F0.wireOp",EDGE,"E13.7.0.1"),sQuery(id+"F0.wireOp",EDGE,"E13.7.0.2"),sQuery(id+"F0.wireOp",EDGE,"E13.7.0.3"),sQuery(id+"F0.wireOp",EDGE,"E13.7.0.4"),sQuery(id+"F0.wireOp",EDGE,"E13.7.0.5"),sQuery(id+"F0.wireOp",EDGE,"E13.8.0.0"),sQuery(id+"F0.wireOp",EDGE,"E13.8.0.1"),sQuery(id+"F0.wireOp",EDGE,"E13.8.0.2"),sQuery(id+"F0.wireOp",EDGE,"E13.8.0.3"),sQuery(id+"F0.wireOp",EDGE,"E13.8.0.4"),sQuery(id+"F0.wireOp",EDGE,"E13.8.0.5"),sQuery(id+"F0.wireOp",EDGE,"E13.9.0.0"),sQuery(id+"F0.wireOp",EDGE,"E13.9.0.1"),sQuery(id+"F0.wireOp",EDGE,"E13.9.0.2"),sQuery(id+"F0.wireOp",EDGE,"E13.9.0.3"),sQuery(id+"F0.wireOp",EDGE,"E13.9.0.4"),sQuery(id+"F0.wireOp",EDGE,"E13.9.0.5"),sQuery(id+"F0.wireOp",EDGE,"E13.10.0.0"),sQuery(id+"F0.wireOp",EDGE,"E13.10.0.1"),sQuery(id+"F0.wireOp",EDGE,"E13.10.0.2"),sQuery(id+"F0.wireOp",EDGE,"E13.10.0.3"),sQuery(id+"F0.wireOp",EDGE,"E13.10.0.4"),sQuery(id+"F0.wireOp",EDGE,"E13.10.0.5"),sQuery(id+"F0.wireOp",EDGE,"E13.11.0.0"),sQuery(id+"F0.wireOp",EDGE,"E13.11.0.1"),sQuery(id+"F0.wireOp",EDGE,"E13.11.0.2"),sQuery(id+"F0.wireOp",EDGE,"E13.11.0.3"),sQuery(id+"F0.wireOp",EDGE,"E13.11.0.4"),sQuery(id+"F0.wireOp",EDGE,"E13.11.0.5"),sQuery(id+"F0.wireOp",EDGE,"E13.12.0.0"),sQuery(id+"F0.wireOp",EDGE,"E13.12.0.1"),sQuery(id+"F0.wireOp",EDGE,"E13.12.0.2"),sQuery(id+"F0.wireOp",EDGE,"E13.12.0.3"),sQuery(id+"F0.wireOp",EDGE,"E13.12.0.4"),sQuery(id+"F0.wireOp",EDGE,"E13.12.0.5"),sQuery(id+"F0.wireOp",EDGE,"E13.13.0.0"),sQuery(id+"F0.wireOp",EDGE,"E13.13.0.1"),sQuery(id+"F0.wireOp",EDGE,"E13.13.0.2"),sQuery(id+"F0.wireOp",EDGE,"E13.13.0.3"),sQuery(id+"F0.wireOp",EDGE,"E13.13.0.4"),sQuery(id+"F0.wireOp",EDGE,"E13.13.0.5"),sQuery(id+"F0.wireOp",EDGE,"E13.14.0.0"),sQuery(id+"F0.wireOp",EDGE,"E13.14.0.1"),sQuery(id+"F0.wireOp",EDGE,"E13.14.0.2"),sQuery(id+"F0.wireOp",EDGE,"E13.14.0.3"),sQuery(id+"F0.wireOp",EDGE,"E13.14.0.4"),sQuery(id+"F0.wireOp",EDGE,"E13.14.0.5"),sQuery(id+"F0.wireOp",EDGE,"E13.15.0.0"),sQuery(id+"F0.wireOp",EDGE,"E13.15.0.1"),sQuery(id+"F0.wireOp",EDGE,"E13.15.0.2"),sQuery(id+"F0.wireOp",EDGE,"E13.15.0.3"),sQuery(id+"F0.wireOp",EDGE,"E13.15.0.4"),sQuery(id+"F0.wireOp",EDGE,"E13.15.0.5"),sQuery(id+"F0.wireOp",EDGE,"E13.16.0.0"),sQuery(id+"F0.wireOp",EDGE,"E13.16.0.1"),sQuery(id+"F0.wireOp",EDGE,"E13.16.0.2"),sQuery(id+"F0.wireOp",EDGE,"E13.16.0.3"),sQuery(id+"F0.wireOp",EDGE,"E13.16.0.4"),sQuery(id+"F0.wireOp",EDGE,"E13.16.0.5"),sQuery(id+"F0.wireOp",EDGE,"E13.17.0.0"),sQuery(id+"F0.wireOp",EDGE,"E13.17.0.1"),sQuery(id+"F0.wireOp",EDGE,"E13.17.0.2"),sQuery(id+"F0.wireOp",EDGE,"E13.17.0.3"),sQuery(id+"F0.wireOp",EDGE,"E13.17.0.4"),sQuery(id+"F0.wireOp",EDGE,"E13.17.0.5"),sQuery(id+"F0.wireOp",EDGE,"E13.18.0.0"),sQuery(id+"F0.wireOp",EDGE,"E13.18.0.1"),sQuery(id+"F0.wireOp",EDGE,"E13.18.0.2"),sQuery(id+"F0.wireOp",EDGE,"E13.18.0.3"),sQuery(id+"F0.wireOp",EDGE,"E13.18.0.4"),sQuery(id+"F0.wireOp",EDGE,"E13.18.0.5"),sQuery(id+"F0.wireOp",EDGE,"E13.19.0.0"),sQuery(id+"F0.wireOp",EDGE,"E13.19.0.1"),sQuery(id+"F0.wireOp",EDGE,"E13.19.0.2"),sQuery(id+"F0.wireOp",EDGE,"E13.19.0.3"),sQuery(id+"F0.wireOp",EDGE,"E13.19.0.4"),sQuery(id+"F0.wireOp",EDGE,"E13.19.0.5"),sQuery(id+"F0.wireOp",EDGE,"E13.20.0.0"),sQuery(id+"F0.wireOp",EDGE,"E13.20.0.1"),sQuery(id+"F0.wireOp",EDGE,"E13.20.0.2"),sQuery(id+"F0.wireOp",EDGE,"E13.20.0.3"),sQuery(id+"F0.wireOp",EDGE,"E13.20.0.4"),sQuery(id+"F0.wireOp",EDGE,"E13.20.0.5"),sQuery(id+"F0.wireOp",EDGE,"E13.21.0.0"),sQuery(id+"F0.wireOp",EDGE,"E13.21.0.1"),sQuery(id+"F0.wireOp",EDGE,"E13.21.0.2"),sQuery(id+"F0.wireOp",EDGE,"E13.21.0.3"),sQuery(id+"F0.wireOp",EDGE,"E13.21.0.4"),sQuery(id+"F0.wireOp",EDGE,"E13.21.0.5"),sQuery(id+"F0.wireOp",EDGE,"E13.22.0.0"),sQuery(id+"F0.wireOp",EDGE,"E13.22.0.1"),sQuery(id+"F0.wireOp",EDGE,"E13.22.0.2"),sQuery(id+"F0.wireOp",EDGE,"E13.22.0.3"),sQuery(id+"F0.wireOp",EDGE,"E13.22.0.4"),sQuery(id+"F0.wireOp",EDGE,"E13.22.0.5"),sQuery(id+"F0.wireOp",EDGE,"E13.23.0.0"),sQuery(id+"F0.wireOp",EDGE,"E13.23.0.1"),sQuery(id+"F0.wireOp",EDGE,"E13.23.0.2"),sQuery(id+"F0.wireOp",EDGE,"E13.23.0.3"),sQuery(id+"F0.wireOp",EDGE,"E13.23.0.4"),sQuery(id+"F0.wireOp",EDGE,"E13.23.0.5"),sQuery(id+"F0.wireOp",EDGE,"E13.24.0.0"),sQuery(id+"F0.wireOp",EDGE,"E13.24.0.1"),sQuery(id+"F0.wireOp",EDGE,"E13.24.0.2"),sQuery(id+"F0.wireOp",EDGE,"E13.24.0.3"),sQuery(id+"F0.wireOp",EDGE,"E13.24.0.4"),sQuery(id+"F0.wireOp",EDGE,"E13.24.0.5"),sQuery(id+"F0.wireOp",EDGE,"E13.25.0.0"),sQuery(id+"F0.wireOp",EDGE,"E13.25.0.1"),sQuery(id+"F0.wireOp",EDGE,"E13.25.0.2"),sQuery(id+"F0.wireOp",EDGE,"E13.25.0.3"),sQuery(id+"F0.wireOp",EDGE,"E13.25.0.4"),sQuery(id+"F0.wireOp",EDGE,"E13.25.0.5"),sQuery(id+"F0.wireOp",EDGE,"E13.26.0.0"),sQuery(id+"F0.wireOp",EDGE,"E13.26.0.1"),sQuery(id+"F0.wireOp",EDGE,"E13.26.0.2"),sQuery(id+"F0.wireOp",EDGE,"E13.26.0.3"),sQuery(id+"F0.wireOp",EDGE,"E13.26.0.4"),sQuery(id+"F0.wireOp",EDGE,"E13.26.0.5"),sQuery(id+"F0.wireOp",EDGE,"E13.27.0.0"),sQuery(id+"F0.wireOp",EDGE,"E13.27.0.1"),sQuery(id+"F0.wireOp",EDGE,"E13.27.0.2"),sQuery(id+"F0.wireOp",EDGE,"E13.27.0.3"),sQuery(id+"F0.wireOp",EDGE,"E13.27.0.4"),sQuery(id+"F0.wireOp",EDGE,"E13.27.0.5"),sQuery(id+"F0.wireOp",EDGE,"E13.28.0.0"),sQuery(id+"F0.wireOp",EDGE,"E13.28.0.1"),sQuery(id+"F0.wireOp",EDGE,"E13.28.0.2"),sQuery(id+"F0.wireOp",EDGE,"E13.28.0.3"),sQuery(id+"F0.wireOp",EDGE,"E13.28.0.4"),sQuery(id+"F0.wireOp",EDGE,"E13.28.0.5"),sQuery(id+"F0.wireOp",EDGE,"E13.29.0.0"),sQuery(id+"F0.wireOp",EDGE,"E13.29.0.1"),sQuery(id+"F0.wireOp",EDGE,"E13.29.0.2"),sQuery(id+"F0.wireOp",EDGE,"E13.29.0.3"),sQuery(id+"F0.wireOp",EDGE,"E13.29.0.4"),sQuery(id+"F0.wireOp",EDGE,"E13.29.0.5"),sQuery(id+"F0.wireOp",EDGE,"E13.30.0.0"),sQuery(id+"F0.wireOp",EDGE,"E13.30.0.1"),sQuery(id+"F0.wireOp",EDGE,"E13.30.0.2"),sQuery(id+"F0.wireOp",EDGE,"E13.30.0.3"),sQuery(id+"F0.wireOp",EDGE,"E13.30.0.4"),sQuery(id+"F0.wireOp",EDGE,"E13.30.0.5"),sQuery(id+"F0.wireOp",EDGE,"E13.31.0.0"),sQuery(id+"F0.wireOp",EDGE,"E13.31.0.1"),sQuery(id+"F0.wireOp",EDGE,"E13.31.0.2"),sQuery(id+"F0.wireOp",EDGE,"E13.31.0.3"),sQuery(id+"F0.wireOp",EDGE,"E13.31.0.4"),sQuery(id+"F0.wireOp",EDGE,"E13.31.0.5"),sQuery(id+"F0.wireOp",EDGE,"E14"),sQuery(id+"F0.wireOp",EDGE,"E15"),sQuery(id+"F0.wireOp",EDGE,"E16")])],"isStart":false});
            var sketch = newSketch(context, id + "F4", { "sketchPlane" : qUnion([Q0])});
            skPoint(sketch, "E23.0", {"position": v(40.64, -2.5) * mm});
            skLineSegment(sketch, "E24.0", {"start": v(-54.36, -5) * mm, "end": v(40.64, -5) * mm});
            skLineSegment(sketch, "E25", {"start": v(40.64, -2.5) * mm, "end": v(43.48, -2.5) * mm, "construction": true});
            skArc(sketch, "E26", {"start": v(42.5, -4.07) * mm, "mid": v(43.22, -3.42) * mm, "end": v(43.48, -2.5) * mm});
            skLineSegment(sketch, "E27", {"start": v(42.5, -4.07) * mm, "end": v(40.64, -5) * mm});
            skCircle(sketch, "E28", {"center": v(41.73, -2.5) * mm, "radius": 1 * mm});
            skArc(sketch, "E29.MirrorCS", {"start": v(42.5, -0.93) * mm, "mid": v(43.22, -1.58) * mm, "end": v(43.48, -2.5) * mm});
            skLineSegment(sketch, "E30.MirrorCS", {"start": v(42.5, -0.93) * mm, "end": v(40.64, 0) * mm});
            skSolve(sketch);
        }
        {
            var Q0;
            Q0=makeQuery(id+"F4.imprint","IMPRINT",FACE,{"disambiguationData":[TD([[makeQuery(id+"F4.imprint","IMPRINT",EDGE,{"derivedFrom":sQuery(id+"F4.wireOp",EDGE,"E26")}),1.0]])]});
            var Q1;
            Q1=makeQuery(id+"F1.opExtrude","CAP_FACE",FACE,{"disambiguationData":[OSD([sQuery(id+"F0.wireOp",EDGE,"E1"),sQuery(id+"F0.wireOp",EDGE,"E5"),sQuery(id+"F0.wireOp",EDGE,"E6"),sQuery(id+"F0.wireOp",EDGE,"E7"),sQuery(id+"F0.wireOp",EDGE,"E8"),sQuery(id+"F0.wireOp",EDGE,"E11"),sQuery(id+"F0.wireOp",EDGE,"E12"),sQuery(id+"F0.wireOp",EDGE,"E13.1.0.0"),sQuery(id+"F0.wireOp",EDGE,"E13.1.0.1"),sQuery(id+"F0.wireOp",EDGE,"E13.1.0.2"),sQuery(id+"F0.wireOp",EDGE,"E13.1.0.3"),sQuery(id+"F0.wireOp",EDGE,"E13.1.0.4"),sQuery(id+"F0.wireOp",EDGE,"E13.1.0.5"),sQuery(id+"F0.wireOp",EDGE,"E13.2.0.0"),sQuery(id+"F0.wireOp",EDGE,"E13.2.0.1"),sQuery(id+"F0.wireOp",EDGE,"E13.2.0.2"),sQuery(id+"F0.wireOp",EDGE,"E13.2.0.3"),sQuery(id+"F0.wireOp",EDGE,"E13.2.0.4"),sQuery(id+"F0.wireOp",EDGE,"E13.2.0.5"),sQuery(id+"F0.wireOp",EDGE,"E13.3.0.0"),sQuery(id+"F0.wireOp",EDGE,"E13.3.0.1"),sQuery(id+"F0.wireOp",EDGE,"E13.3.0.2"),sQuery(id+"F0.wireOp",EDGE,"E13.3.0.3"),sQuery(id+"F0.wireOp",EDGE,"E13.3.0.4"),sQuery(id+"F0.wireOp",EDGE,"E13.3.0.5"),sQuery(id+"F0.wireOp",EDGE,"E13.4.0.0"),sQuery(id+"F0.wireOp",EDGE,"E13.4.0.1"),sQuery(id+"F0.wireOp",EDGE,"E13.4.0.2"),sQuery(id+"F0.wireOp",EDGE,"E13.4.0.3"),sQuery(id+"F0.wireOp",EDGE,"E13.4.0.4"),sQuery(id+"F0.wireOp",EDGE,"E13.4.0.5"),sQuery(id+"F0.wireOp",EDGE,"E13.5.0.0"),sQuery(id+"F0.wireOp",EDGE,"E13.5.0.1"),sQuery(id+"F0.wireOp",EDGE,"E13.5.0.2"),sQuery(id+"F0.wireOp",EDGE,"E13.5.0.3"),sQuery(id+"F0.wireOp",EDGE,"E13.5.0.4"),sQuery(id+"F0.wireOp",EDGE,"E13.5.0.5"),sQuery(id+"F0.wireOp",EDGE,"E13.6.0.0"),sQuery(id+"F0.wireOp",EDGE,"E13.6.0.1"),sQuery(id+"F0.wireOp",EDGE,"E13.6.0.2"),sQuery(id+"F0.wireOp",EDGE,"E13.6.0.3"),sQuery(id+"F0.wireOp",EDGE,"E13.6.0.4"),sQuery(id+"F0.wireOp",EDGE,"E13.6.0.5"),sQuery(id+"F0.wireOp",EDGE,"E13.7.0.0"),sQuery(id+"F0.wireOp",EDGE,"E13.7.0.1"),sQuery(id+"F0.wireOp",EDGE,"E13.7.0.2"),sQuery(id+"F0.wireOp",EDGE,"E13.7.0.3"),sQuery(id+"F0.wireOp",EDGE,"E13.7.0.4"),sQuery(id+"F0.wireOp",EDGE,"E13.7.0.5"),sQuery(id+"F0.wireOp",EDGE,"E13.8.0.0"),sQuery(id+"F0.wireOp",EDGE,"E13.8.0.1"),sQuery(id+"F0.wireOp",EDGE,"E13.8.0.2"),sQuery(id+"F0.wireOp",EDGE,"E13.8.0.3"),sQuery(id+"F0.wireOp",EDGE,"E13.8.0.4"),sQuery(id+"F0.wireOp",EDGE,"E13.8.0.5"),sQuery(id+"F0.wireOp",EDGE,"E13.9.0.0"),sQuery(id+"F0.wireOp",EDGE,"E13.9.0.1"),sQuery(id+"F0.wireOp",EDGE,"E13.9.0.2"),sQuery(id+"F0.wireOp",EDGE,"E13.9.0.3"),sQuery(id+"F0.wireOp",EDGE,"E13.9.0.4"),sQuery(id+"F0.wireOp",EDGE,"E13.9.0.5"),sQuery(id+"F0.wireOp",EDGE,"E13.10.0.0"),sQuery(id+"F0.wireOp",EDGE,"E13.10.0.1"),sQuery(id+"F0.wireOp",EDGE,"E13.10.0.2"),sQuery(id+"F0.wireOp",EDGE,"E13.10.0.3"),sQuery(id+"F0.wireOp",EDGE,"E13.10.0.4"),sQuery(id+"F0.wireOp",EDGE,"E13.10.0.5"),sQuery(id+"F0.wireOp",EDGE,"E13.11.0.0"),sQuery(id+"F0.wireOp",EDGE,"E13.11.0.1"),sQuery(id+"F0.wireOp",EDGE,"E13.11.0.2"),sQuery(id+"F0.wireOp",EDGE,"E13.11.0.3"),sQuery(id+"F0.wireOp",EDGE,"E13.11.0.4"),sQuery(id+"F0.wireOp",EDGE,"E13.11.0.5"),sQuery(id+"F0.wireOp",EDGE,"E13.12.0.0"),sQuery(id+"F0.wireOp",EDGE,"E13.12.0.1"),sQuery(id+"F0.wireOp",EDGE,"E13.12.0.2"),sQuery(id+"F0.wireOp",EDGE,"E13.12.0.3"),sQuery(id+"F0.wireOp",EDGE,"E13.12.0.4"),sQuery(id+"F0.wireOp",EDGE,"E13.12.0.5"),sQuery(id+"F0.wireOp",EDGE,"E13.13.0.0"),sQuery(id+"F0.wireOp",EDGE,"E13.13.0.1"),sQuery(id+"F0.wireOp",EDGE,"E13.13.0.2"),sQuery(id+"F0.wireOp",EDGE,"E13.13.0.3"),sQuery(id+"F0.wireOp",EDGE,"E13.13.0.4"),sQuery(id+"F0.wireOp",EDGE,"E13.13.0.5"),sQuery(id+"F0.wireOp",EDGE,"E13.14.0.0"),sQuery(id+"F0.wireOp",EDGE,"E13.14.0.1"),sQuery(id+"F0.wireOp",EDGE,"E13.14.0.2"),sQuery(id+"F0.wireOp",EDGE,"E13.14.0.3"),sQuery(id+"F0.wireOp",EDGE,"E13.14.0.4"),sQuery(id+"F0.wireOp",EDGE,"E13.14.0.5"),sQuery(id+"F0.wireOp",EDGE,"E13.15.0.0"),sQuery(id+"F0.wireOp",EDGE,"E13.15.0.1"),sQuery(id+"F0.wireOp",EDGE,"E13.15.0.2"),sQuery(id+"F0.wireOp",EDGE,"E13.15.0.3"),sQuery(id+"F0.wireOp",EDGE,"E13.15.0.4"),sQuery(id+"F0.wireOp",EDGE,"E13.15.0.5"),sQuery(id+"F0.wireOp",EDGE,"E13.16.0.0"),sQuery(id+"F0.wireOp",EDGE,"E13.16.0.1"),sQuery(id+"F0.wireOp",EDGE,"E13.16.0.2"),sQuery(id+"F0.wireOp",EDGE,"E13.16.0.3"),sQuery(id+"F0.wireOp",EDGE,"E13.16.0.4"),sQuery(id+"F0.wireOp",EDGE,"E13.16.0.5"),sQuery(id+"F0.wireOp",EDGE,"E13.17.0.0"),sQuery(id+"F0.wireOp",EDGE,"E13.17.0.1"),sQuery(id+"F0.wireOp",EDGE,"E13.17.0.2"),sQuery(id+"F0.wireOp",EDGE,"E13.17.0.3"),sQuery(id+"F0.wireOp",EDGE,"E13.17.0.4"),sQuery(id+"F0.wireOp",EDGE,"E13.17.0.5"),sQuery(id+"F0.wireOp",EDGE,"E13.18.0.0"),sQuery(id+"F0.wireOp",EDGE,"E13.18.0.1"),sQuery(id+"F0.wireOp",EDGE,"E13.18.0.2"),sQuery(id+"F0.wireOp",EDGE,"E13.18.0.3"),sQuery(id+"F0.wireOp",EDGE,"E13.18.0.4"),sQuery(id+"F0.wireOp",EDGE,"E13.18.0.5"),sQuery(id+"F0.wireOp",EDGE,"E13.19.0.0"),sQuery(id+"F0.wireOp",EDGE,"E13.19.0.1"),sQuery(id+"F0.wireOp",EDGE,"E13.19.0.2"),sQuery(id+"F0.wireOp",EDGE,"E13.19.0.3"),sQuery(id+"F0.wireOp",EDGE,"E13.19.0.4"),sQuery(id+"F0.wireOp",EDGE,"E13.19.0.5"),sQuery(id+"F0.wireOp",EDGE,"E13.20.0.0"),sQuery(id+"F0.wireOp",EDGE,"E13.20.0.1"),sQuery(id+"F0.wireOp",EDGE,"E13.20.0.2"),sQuery(id+"F0.wireOp",EDGE,"E13.20.0.3"),sQuery(id+"F0.wireOp",EDGE,"E13.20.0.4"),sQuery(id+"F0.wireOp",EDGE,"E13.20.0.5"),sQuery(id+"F0.wireOp",EDGE,"E13.21.0.0"),sQuery(id+"F0.wireOp",EDGE,"E13.21.0.1"),sQuery(id+"F0.wireOp",EDGE,"E13.21.0.2"),sQuery(id+"F0.wireOp",EDGE,"E13.21.0.3"),sQuery(id+"F0.wireOp",EDGE,"E13.21.0.4"),sQuery(id+"F0.wireOp",EDGE,"E13.21.0.5"),sQuery(id+"F0.wireOp",EDGE,"E13.22.0.0"),sQuery(id+"F0.wireOp",EDGE,"E13.22.0.1"),sQuery(id+"F0.wireOp",EDGE,"E13.22.0.2"),sQuery(id+"F0.wireOp",EDGE,"E13.22.0.3"),sQuery(id+"F0.wireOp",EDGE,"E13.22.0.4"),sQuery(id+"F0.wireOp",EDGE,"E13.22.0.5"),sQuery(id+"F0.wireOp",EDGE,"E13.23.0.0"),sQuery(id+"F0.wireOp",EDGE,"E13.23.0.1"),sQuery(id+"F0.wireOp",EDGE,"E13.23.0.2"),sQuery(id+"F0.wireOp",EDGE,"E13.23.0.3"),sQuery(id+"F0.wireOp",EDGE,"E13.23.0.4"),sQuery(id+"F0.wireOp",EDGE,"E13.23.0.5"),sQuery(id+"F0.wireOp",EDGE,"E13.24.0.0"),sQuery(id+"F0.wireOp",EDGE,"E13.24.0.1"),sQuery(id+"F0.wireOp",EDGE,"E13.24.0.2"),sQuery(id+"F0.wireOp",EDGE,"E13.24.0.3"),sQuery(id+"F0.wireOp",EDGE,"E13.24.0.4"),sQuery(id+"F0.wireOp",EDGE,"E13.24.0.5"),sQuery(id+"F0.wireOp",EDGE,"E13.25.0.0"),sQuery(id+"F0.wireOp",EDGE,"E13.25.0.1"),sQuery(id+"F0.wireOp",EDGE,"E13.25.0.2"),sQuery(id+"F0.wireOp",EDGE,"E13.25.0.3"),sQuery(id+"F0.wireOp",EDGE,"E13.25.0.4"),sQuery(id+"F0.wireOp",EDGE,"E13.25.0.5"),sQuery(id+"F0.wireOp",EDGE,"E13.26.0.0"),sQuery(id+"F0.wireOp",EDGE,"E13.26.0.1"),sQuery(id+"F0.wireOp",EDGE,"E13.26.0.2"),sQuery(id+"F0.wireOp",EDGE,"E13.26.0.3"),sQuery(id+"F0.wireOp",EDGE,"E13.26.0.4"),sQuery(id+"F0.wireOp",EDGE,"E13.26.0.5"),sQuery(id+"F0.wireOp",EDGE,"E13.27.0.0"),sQuery(id+"F0.wireOp",EDGE,"E13.27.0.1"),sQuery(id+"F0.wireOp",EDGE,"E13.27.0.2"),sQuery(id+"F0.wireOp",EDGE,"E13.27.0.3"),sQuery(id+"F0.wireOp",EDGE,"E13.27.0.4"),sQuery(id+"F0.wireOp",EDGE,"E13.27.0.5"),sQuery(id+"F0.wireOp",EDGE,"E13.28.0.0"),sQuery(id+"F0.wireOp",EDGE,"E13.28.0.1"),sQuery(id+"F0.wireOp",EDGE,"E13.28.0.2"),sQuery(id+"F0.wireOp",EDGE,"E13.28.0.3"),sQuery(id+"F0.wireOp",EDGE,"E13.28.0.4"),sQuery(id+"F0.wireOp",EDGE,"E13.28.0.5"),sQuery(id+"F0.wireOp",EDGE,"E13.29.0.0"),sQuery(id+"F0.wireOp",EDGE,"E13.29.0.1"),sQuery(id+"F0.wireOp",EDGE,"E13.29.0.2"),sQuery(id+"F0.wireOp",EDGE,"E13.29.0.3"),sQuery(id+"F0.wireOp",EDGE,"E13.29.0.4"),sQuery(id+"F0.wireOp",EDGE,"E13.29.0.5"),sQuery(id+"F0.wireOp",EDGE,"E13.30.0.0"),sQuery(id+"F0.wireOp",EDGE,"E13.30.0.1"),sQuery(id+"F0.wireOp",EDGE,"E13.30.0.2"),sQuery(id+"F0.wireOp",EDGE,"E13.30.0.3"),sQuery(id+"F0.wireOp",EDGE,"E13.30.0.4"),sQuery(id+"F0.wireOp",EDGE,"E13.30.0.5"),sQuery(id+"F0.wireOp",EDGE,"E13.31.0.0"),sQuery(id+"F0.wireOp",EDGE,"E13.31.0.1"),sQuery(id+"F0.wireOp",EDGE,"E13.31.0.2"),sQuery(id+"F0.wireOp",EDGE,"E13.31.0.3"),sQuery(id+"F0.wireOp",EDGE,"E13.31.0.4"),sQuery(id+"F0.wireOp",EDGE,"E13.31.0.5"),sQuery(id+"F0.wireOp",EDGE,"E14"),sQuery(id+"F0.wireOp",EDGE,"E15"),sQuery(id+"F0.wireOp",EDGE,"E16")])],"isStart":true});
            extrude(context, id + "F5", {"entities" : qUnion([Q0]), "operationType" : NewBodyOperationType.ADD, "endBound" : BoundingType.UP_TO_SURFACE, "oppositeDirection" : true, "depth" : 25 * mm, "endBoundEntityFace" : qUnion([Q1]), "offsetDistance" : 25 * mm});
        }
    });
